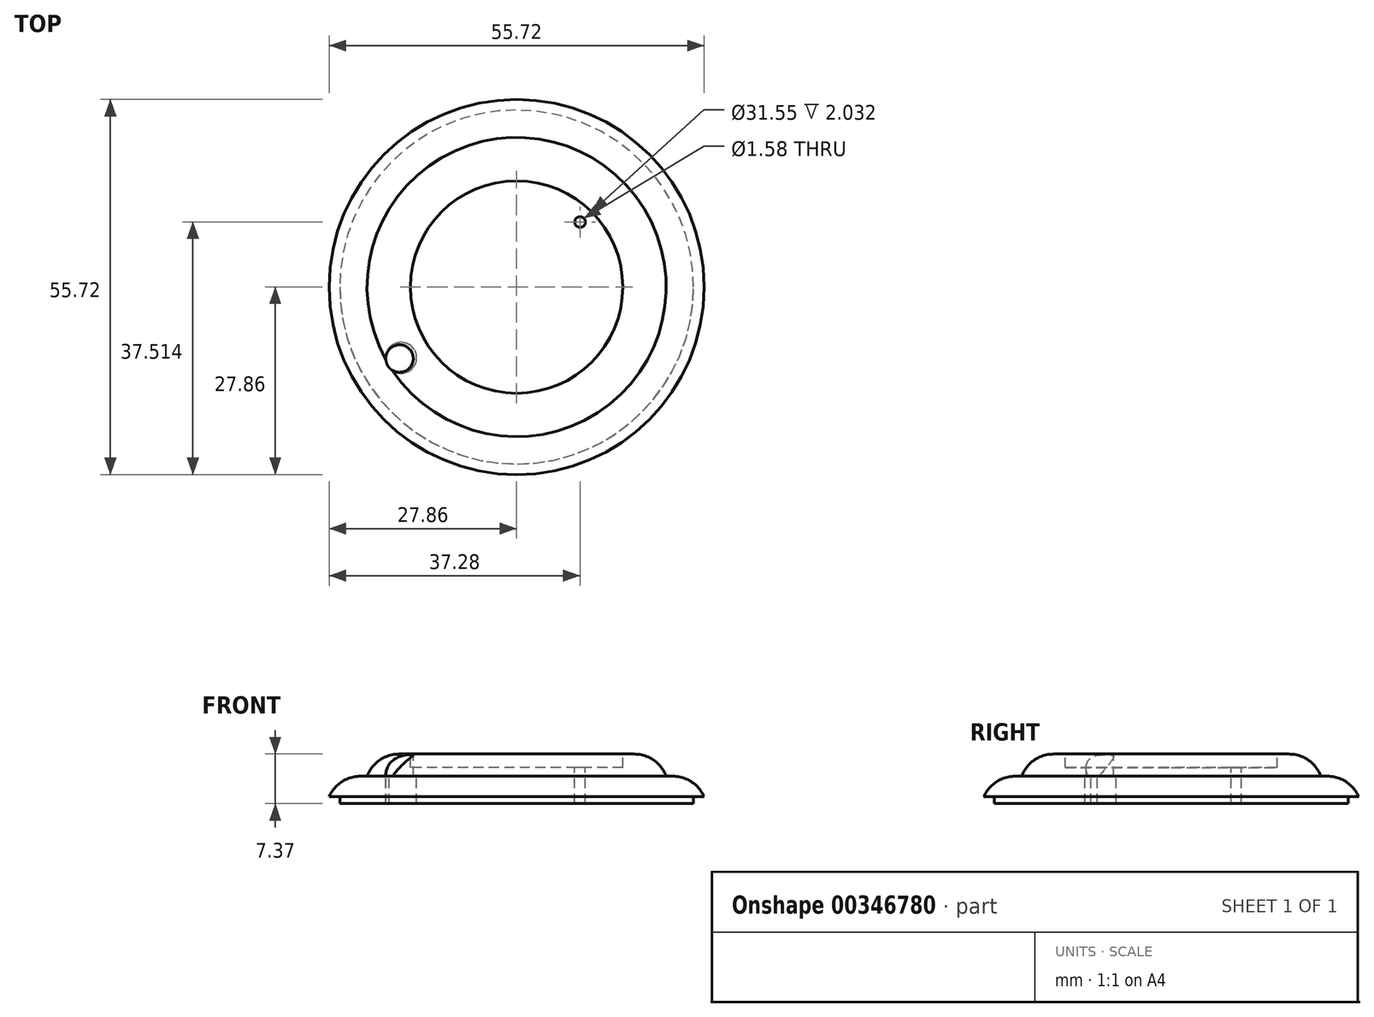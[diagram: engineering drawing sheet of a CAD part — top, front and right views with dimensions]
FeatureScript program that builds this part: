
annotation { "Feature Type Name" : "Feature", "Feature Type Description" : "" }
export const myFeature = defineFeature(function(context is Context, id is Id, definition is map)
    precondition{}
    {
        {
            var Q0;
            Q0=qCreatedBy(makeId("Top.planeOp"),FACE);
            var sketch = newSketch(context, id + "F0", { "sketchPlane" : qUnion([Q0])});
            skCircle(sketch, "E0", {"center": v(0, 0) * mm, "radius": 27.86 * mm});
            skSolve(sketch);
        }
        {
            var Q0;
            Q0=makeQuery(id+"F0.imprint","IMPRINT",FACE,{"disambiguationData":[TD([[makeQuery(id+"F0.imprint","IMPRINT",EDGE,{"derivedFrom":sQuery(id+"F0.wireOp",EDGE,"E0")}),1.0]])]});
            extrude(context, id + "F1", {"entities" : qUnion([Q0]), "depth" : 3.05 * mm});
        }
        {
            var Q0;
            Q0=makeQuery(id+"F1.opExtrude","CAP_EDGE",EDGE,{"disambiguationData":[OSD([sQuery(id+"F0.wireOp",EDGE,"E0")])],"isStart":false});
            fillet(context, id + "F2", {"entities" : qUnion([Q0]), "radius" : 5.08 * mm, "tangentPropagation" : true, "allowEdgeOverflow" : false});
        }
        {
            var Q0;
            Q0=makeQuery(id+"F1.opExtrude","CAP_FACE",FACE,{"disambiguationData":[OSD([sQuery(id+"F0.wireOp",EDGE,"E0")])],"isStart":true});
            var sketch = newSketch(context, id + "F3", { "sketchPlane" : qUnion([Q0])});
            skSolve(sketch);
        }
        {
            var Q0;
            {var subQ0=sQuery(id+"F0.wireOp",EDGE,"E0");Q0=makeQuery(id+"F3.imprint","IMPRINT",FACE,{"disambiguationData":[TD([[makeQuery(id+"F3.imprint","IMPRINT",EDGE,{"derivedFrom":makeQuery(id+"F2.opFillet","BLEND_EDGE",EDGE,{"blendedFrom":[makeQuery(id+"F1.opExtrude","CAP_EDGE",EDGE,{"disambiguationData":[OSD([subQ0])],"isStart":false}),makeQuery(id+"F1.opExtrude","CAP_FACE",FACE,{"disambiguationData":[OSD([subQ0])],"isStart":true})],"blendedInto":[makeQuery(id+"F1.opExtrude","CAP_FACE",FACE,{"disambiguationData":[OSD([subQ0])],"isStart":true})]})}),-1.0]])]});}
            var sketch = newSketch(context, id + "F4", { "sketchPlane" : qUnion([Q0])});
            skCircle(sketch, "E1", {"center": v(0, 0) * mm, "radius": 26.28 * mm});
            skSolve(sketch);
        }
        {
            var Q0;
            Q0 = qSketchRegion(id + "F4", true);
            extrude(context, id + "F5", {"entities" : qUnion([Q0]), "operationType" : NewBodyOperationType.ADD, "depth" : 1.02 * mm});
        }
        {
            var Q0;
            Q0=makeQuery(id+"F1.opExtrude","CAP_FACE",FACE,{"disambiguationData":[OSD([sQuery(id+"F0.wireOp",EDGE,"E0")])],"isStart":false});
            var sketch = newSketch(context, id + "F6", { "sketchPlane" : qUnion([Q0])});
            skCircle(sketch, "E2", {"center": v(0, 0) * mm, "radius": 22.22 * mm});
            skSolve(sketch);
        }
        {
            var Q0;
            Q0=makeQuery(id+"F6.imprint","IMPRINT",FACE,{"disambiguationData":[TD([[makeQuery(id+"F6.imprint","IMPRINT",EDGE,{"derivedFrom":sQuery(id+"F6.wireOp",EDGE,"E2")}),1.0]])]});
            extrude(context, id + "F7", {"entities" : qUnion([Q0]), "operationType" : NewBodyOperationType.ADD, "depth" : 3.3 * mm});
        }
        {
            var Q0;
            Q0=makeQuery(id+"F7.opExtrude","CAP_EDGE",EDGE,{"disambiguationData":[OSD([sQuery(id+"F6.wireOp",EDGE,"E2")])],"isStart":false});
            fillet(context, id + "F8", {"entities" : qUnion([Q0]), "radius" : 5.08 * mm, "tangentPropagation" : true, "allowEdgeOverflow" : false});
        }
        {
            var Q0;
            Q0=makeQuery(id+"F7.opExtrude","CAP_FACE",FACE,{"disambiguationData":[OSD([sQuery(id+"F6.wireOp",EDGE,"E2")])],"isStart":false});
            var sketch = newSketch(context, id + "F9", { "sketchPlane" : qUnion([Q0])});
            skCircle(sketch, "E3", {"center": v(0, 0) * mm, "radius": 15.77 * mm});
            skSolve(sketch);
        }
        {
            var Q0;
            Q0=makeQuery(id+"F9.imprint","IMPRINT",FACE,{"disambiguationData":[TD([[makeQuery(id+"F9.imprint","IMPRINT",EDGE,{"derivedFrom":sQuery(id+"F9.wireOp",EDGE,"E3")}),1.0]])]});
            extrude(context, id + "F10", {"entities" : qUnion([Q0]), "operationType" : NewBodyOperationType.REMOVE, "oppositeDirection" : true, "depth" : 2.03 * mm});
        }
        {
            var Q0;
            Q0=makeQuery(id+"F1.opExtrude","CAP_FACE",FACE,{"disambiguationData":[OSD([sQuery(id+"F0.wireOp",EDGE,"E0")])],"isStart":false});
            var sketch = newSketch(context, id + "F11", { "sketchPlane" : qUnion([Q0])});
            skCircle(sketch, "E4", {"center": v(-17.16, -10.5) * mm, "radius": 2.3 * mm});
            skSolve(sketch);
        }
        {
            var Q0;
            Q0 = qSketchRegion(id + "F11", true);
            extrude(context, id + "F12", {"entities" : qUnion([Q0]), "operationType" : NewBodyOperationType.REMOVE, "oppositeDirection" : true, "depth" : 21.34 * mm});
        }
        {
            var Q0;
            Q0=makeQuery(id+"F7.opExtrude","CAP_FACE",FACE,{"disambiguationData":[OSD([sQuery(id+"F6.wireOp",EDGE,"E2")])],"isStart":false});
            var sketch = newSketch(context, id + "F13", { "sketchPlane" : qUnion([Q0])});
            skCircle(sketch, "E5", {"center": v(-17.39, -10.62) * mm, "radius": 2.05 * mm});
            skSolve(sketch);
        }
        {
            var Q0;
            Q0 = qSketchRegion(id + "F13", true);
            extrude(context, id + "F14", {"entities" : qUnion([Q0]), "operationType" : NewBodyOperationType.REMOVE, "oppositeDirection" : true, "depth" : 25.4 * mm});
        }
        {
            var Q0;
            Q0=makeQuery(id+"F10.boolean.opBoolean","COPY",FACE,{"derivedFrom":makeQuery(id+"F10.opExtrude","CAP_FACE",FACE,{"disambiguationData":[OSD([sQuery(id+"F9.wireOp",EDGE,"E3")])],"isStart":false})});
            var sketch = newSketch(context, id + "F15", { "sketchPlane" : qUnion([Q0])});
            skCircle(sketch, "E6", {"center": v(9.42, 9.65) * mm, "radius": 0.8 * mm});
            skSolve(sketch);
        }
        {
            var Q0;
            Q0=makeQuery(id+"F15.imprint","IMPRINT",FACE,{"disambiguationData":[TD([[makeQuery(id+"F15.imprint","IMPRINT",EDGE,{"derivedFrom":sQuery(id+"F15.wireOp",EDGE,"E6")}),1.0]])]});
            extrude(context, id + "F16", {"entities" : qUnion([Q0]), "operationType" : NewBodyOperationType.REMOVE, "oppositeDirection" : true, "depth" : 25.4 * mm});
        }
    });
